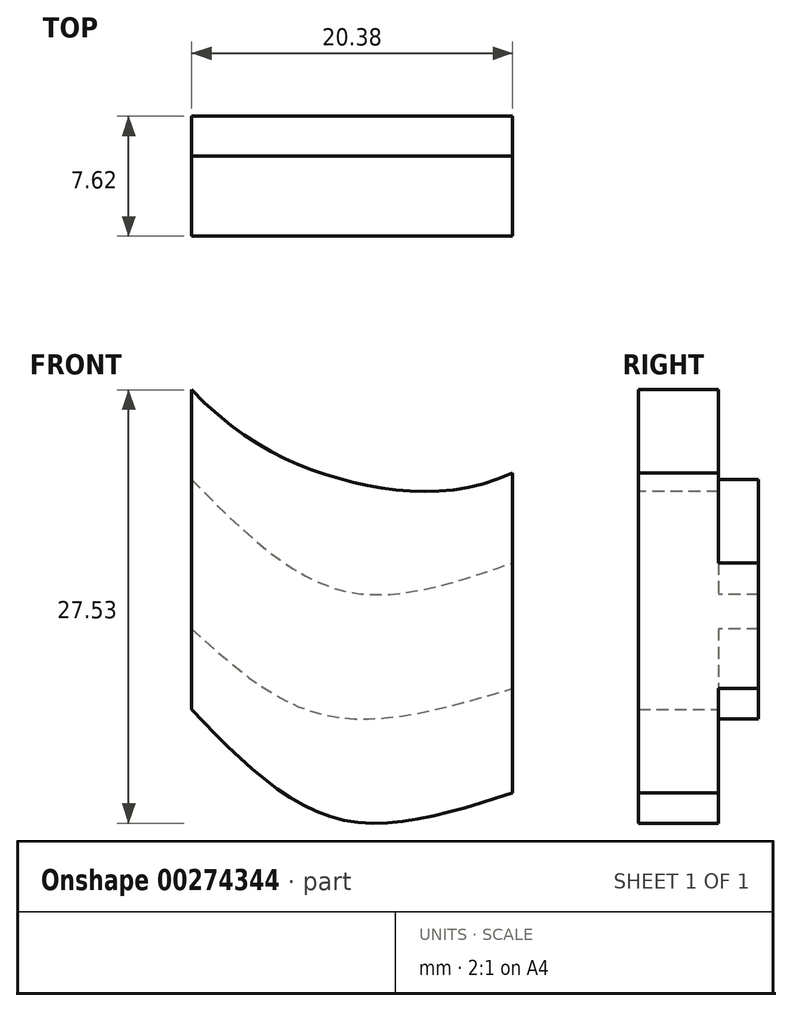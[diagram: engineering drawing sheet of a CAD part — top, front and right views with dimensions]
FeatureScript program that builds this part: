
annotation { "Feature Type Name" : "Feature", "Feature Type Description" : "" }
export const myFeature = defineFeature(function(context is Context, id is Id, definition is map)
    precondition{}
    {
        {
            var Q0;
            Q0=qCreatedBy(makeId("Front.planeOp"),FACE);
            var sketch = newSketch(context, id + "F0", { "sketchPlane" : qUnion([Q0])});
            skLineSegment(sketch, "E0", {"start": v(-69.62, 38.91) * mm, "end": v(-69.62, 18.6) * mm});
            skLineSegment(sketch, "E1", {"start": v(-49.24, 33.63) * mm, "end": v(-49.24, 13.31) * mm});
            skFitSpline(sketch, "E2", {"points": [v(-69.62, 38.91) * mm, v(-59.43, 33.06) * mm, v(-49.24, 33.63) * mm], "startDerivative": vector(18.88, -19.96) * mm, "endDerivative": vector(21.93, 9.9) * mm});
            skFitSpline(sketch, "E3", {"points": [v(-69.62, 18.6) * mm, v(-60.3, 11.65) * mm, v(-49.24, 13.31) * mm], "startDerivative": vector(17.49, -18.06) * mm, "endDerivative": vector(23.3, 7.59) * mm});
            skFitSpline(sketch, "E4", {"points": [v(-69.62, 33.2) * mm, v(-60, 26.14) * mm, v(-49.24, 27.91) * mm], "startDerivative": vector(18, -18.27) * mm, "endDerivative": vector(22.8, 7.87) * mm});
            skFitSpline(sketch, "E5", {"points": [v(-69.62, 23.73) * mm, v(-61.11, 18.23) * mm, v(-49.24, 19.93) * mm], "startDerivative": vector(16.56, -15) * mm, "endDerivative": vector(24.1, 7.1) * mm});
            skSolve(sketch);
        }
        {
            var Q0;
            Q0=makeQuery(id+"F0.imprint","IMPRINT",FACE,{"disambiguationData":[TD([[makeQuery(id+"F0.imprint","IMPRINT",EDGE,{"derivedFrom":sQuery(id+"F0.wireOp",EDGE,"E0")}),1.0]])]});
            extrude(context, id + "F1", {"entities" : qUnion([Q0]), "depth" : 5.08 * mm});
        }
        {
            var Q0;
            {var subQ0=sQuery(id+"F0.wireOp",EDGE,"E4");Q0=makeQuery(id+"F0.imprint","IMPRINT",FACE,{"disambiguationData":[TD([[makeQuery(id+"F0.imprint","IMPRINT",EDGE,{"derivedFrom":subQ0}),-1.0]])]});}
            extrude(context, id + "F2", {"entities" : qUnion([Q0]), "operationType" : NewBodyOperationType.ADD, "oppositeDirection" : true, "depth" : 2.54 * mm});
        }
    });
